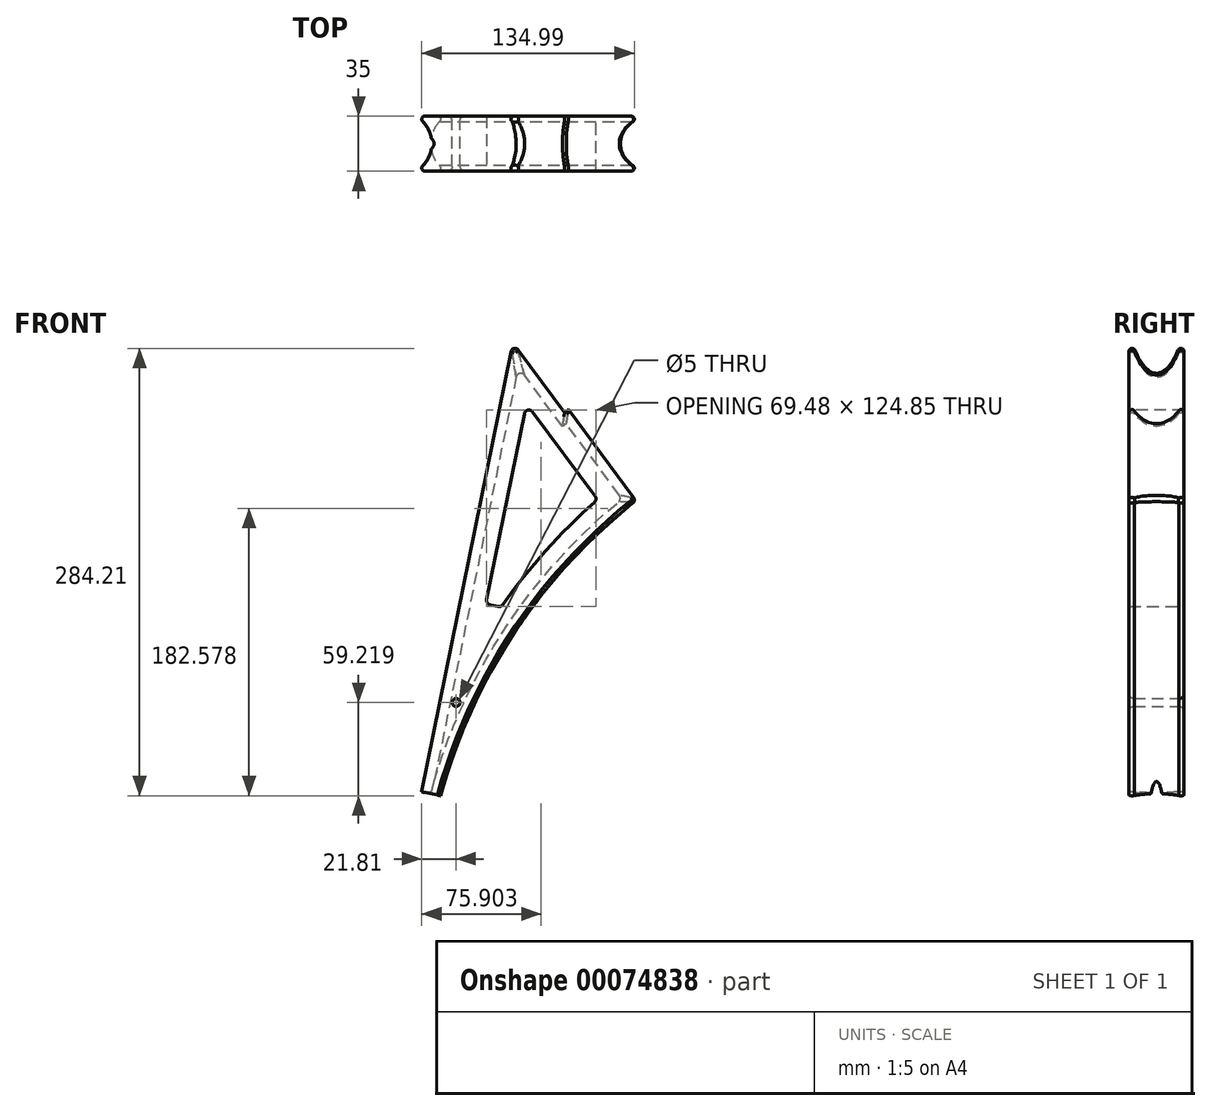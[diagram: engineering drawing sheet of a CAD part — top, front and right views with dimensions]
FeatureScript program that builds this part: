
annotation { "Feature Type Name" : "Feature", "Feature Type Description" : "" }
export const myFeature = defineFeature(function(context is Context, id is Id, definition is map)
    precondition{}
    {
        {
            var Q0;
            Q0=qCreatedBy(makeId("Front.planeOp"),FACE);
            var sketch = newSketch(context, id + "F0", { "sketchPlane" : qUnion([Q0])});
            skLineSegment(sketch, "E0", {"start": v(0, 0) * mm, "end": v(59.65, 294.01) * mm});
            skLineSegment(sketch, "E1", {"start": v(59.65, 294.01) * mm, "end": v(95.36, 245.8) * mm});
            skLineSegment(sketch, "E2", {"start": v(95.36, 245.8) * mm, "end": v(97.77, 247.59) * mm});
            skLineSegment(sketch, "E3", {"start": v(97.77, 247.59) * mm, "end": v(145.26, 183.48) * mm});
            skLineSegment(sketch, "E4", {"start": v(115.54, 184.96) * mm, "end": v(70.32, 246.01) * mm});
            skLineSegment(sketch, "E5", {"start": v(0, 0) * mm, "end": v(19.6, -3.98) * mm});
            skArc(sketch, "E6", {"start": v(145.26, 183.48) * mm, "mid": v(67.14, 100) * mm, "end": v(19.6, -3.98) * mm});
            skLineSegment(sketch, "E7", {"start": v(70.32, 246.01) * mm, "end": v(44.47, 118.6) * mm});
            skLineSegment(sketch, "E8", {"start": v(44.47, 118.6) * mm, "end": v(54.27, 116.62) * mm});
            skArc(sketch, "E9", {"start": v(115.54, 184.96) * mm, "mid": v(82.8, 152.67) * mm, "end": v(54.27, 116.62) * mm});
            skCircle(sketch, "E10", {"center": v(25.65, 56.02) * mm, "radius": 2.5 * mm});
            skSolve(sketch);
        }
        {
            var Q0;
            Q0 = qSketchRegion(id + "F0", true);
            extrude(context, id + "F1", {"entities" : qUnion([Q0]), "depth" : 35 * mm});
        }
        {
            var Q0;
            Q0=makeQuery(id+"F1.opExtrude","SWEPT_FACE",FACE,{"disambiguationData":[OSD([sQuery(id+"F0.wireOp",EDGE,"E5")])]});
            var sketch = newSketch(context, id + "F2", { "sketchPlane" : qUnion([Q0])});
            skArc(sketch, "E11", {"start": v(20, 35) * mm, "mid": v(9.68, 17.5) * mm, "end": v(20, 0) * mm});
            skLineSegment(sketch, "E12", {"start": v(20, 0) * mm, "end": v(20, 35) * mm});
            skSolve(sketch);
        }
        {
            var Q0;
            Q0=makeQuery(id+"F2.imprint","IMPRINT",FACE,{"disambiguationData":[TD([[makeQuery(id+"F2.imprint","IMPRINT",EDGE,{"derivedFrom":sQuery(id+"F2.wireOp",EDGE,"E11")}),1.0]])]});
            var Q1;
            Q1=makeQuery(id+"F1.opExtrude","CAP_EDGE",EDGE,{"disambiguationData":[OSD([sQuery(id+"F0.wireOp",EDGE,"E6")])],"isStart":true});
            var Q2;
            Q2=makeQuery(id+"F1.opExtrude","CAP_EDGE",EDGE,{"disambiguationData":[OSD([sQuery(id+"F0.wireOp",EDGE,"E3")])],"isStart":true});
            var Q3;
            Q3=makeQuery(id+"F1.opExtrude","CAP_EDGE",EDGE,{"disambiguationData":[OSD([sQuery(id+"F0.wireOp",EDGE,"E1")])],"isStart":true});
            var Q4;
            Q4=makeQuery(id+"F1.opExtrude","CAP_EDGE",EDGE,{"disambiguationData":[OSD([sQuery(id+"F0.wireOp",EDGE,"E2")])],"isStart":true});
            var Q5;
            Q5=makeQuery(id+"F1.opExtrude","CAP_EDGE",EDGE,{"disambiguationData":[OSD([sQuery(id+"F0.wireOp",EDGE,"E0")])],"isStart":true});
            sweep(context, id + "F3", {"operationType" : NewBodyOperationType.REMOVE, "profiles" : qUnion([Q0]), "path" : qUnion([Q1, Q2, Q3, Q4, Q5])});
        }
        {
            var Q0;
            Q0=makeQuery(id+"F3.boolean.opBoolean","COPY",FACE,{"derivedFrom":makeQuery(id+"F3.opSweep","CAP_FACE",FACE,{"disambiguationData":[OSD([sQuery(id+"F0.wireOp",EDGE,"E0"),sQuery(id+"F0.wireOp",EDGE,"E5"),sQuery(id+"F2.wireOp",EDGE,"E11"),sQuery(id+"F2.wireOp",EDGE,"E12")])],"isStart":false})});
            extrude(context, id + "F4", {"entities" : qUnion([Q0]), "operationType" : NewBodyOperationType.REMOVE, "oppositeDirection" : true, "depth" : 25 * mm});
        }
        {
            var Q0;
            {var subQ0=sQuery(id+"F2.wireOp",EDGE,"E12");var subQ1=sQuery(id+"F2.wireOp",EDGE,"E11");var subQ2=sQuery(id+"F0.wireOp",EDGE,"E5");var subQ3=sQuery(id+"F0.wireOp",EDGE,"E0");var subQ4=makeQuery(id+"F1.opExtrude","CAP_EDGE",EDGE,{"disambiguationData":[OSD([subQ3])],"isStart":true});Q0=makeQuery(id+"FQC8LGYjpT3Sznm_1.boolean.opBoolean","MERGE",EDGE,{"derivedFrom":[subQ4,makeQuery(id+"FQC8LGYjpT3Sznm_1.opSweep","SWEPT_EDGE",EDGE,{"disambiguationData":[OSD([subQ3,subQ2,subQ1,subQ0]),TDD([subQ4,makeQuery(id+"F2.imprint","INTERSECT",VERTEX,{"derivedFrom":[makeQuery(id+"F1.opExtrude","CAP_EDGE",EDGE,{"disambiguationData":[OSD([subQ2])],"isStart":true}),subQ1,subQ0]})])]})]});}
            var Q1;
            {var subQ0=sQuery(id+"F2.wireOp",EDGE,"E12");var subQ1=sQuery(id+"F2.wireOp",EDGE,"E11");var subQ2=sQuery(id+"F0.wireOp",EDGE,"E5");var subQ3=sQuery(id+"F0.wireOp",EDGE,"E0");Q1=makeQuery(id+"FQC8LGYjpT3Sznm_1.boolean.opBoolean","MERGE",EDGE,{"derivedFrom":[makeQuery(id+"F1.opExtrude","CAP_EDGE",EDGE,{"disambiguationData":[OSD([subQ3])],"isStart":false}),makeQuery(id+"FQC8LGYjpT3Sznm_1.opSweep","SWEPT_EDGE",EDGE,{"disambiguationData":[OSD([subQ3,subQ2,subQ1,subQ0]),TDD([makeQuery(id+"F1.opExtrude","CAP_EDGE",EDGE,{"disambiguationData":[OSD([subQ3])],"isStart":true}),makeQuery(id+"F2.imprint","INTERSECT",VERTEX,{"derivedFrom":[makeQuery(id+"F1.opExtrude","CAP_EDGE",EDGE,{"disambiguationData":[OSD([subQ2])],"isStart":false}),subQ1,subQ0]})])]})]});}
            var Q2;
            {var subQ0=sQuery(id+"F2.wireOp",EDGE,"E12");var subQ1=sQuery(id+"F2.wireOp",EDGE,"E11");var subQ2=sQuery(id+"F0.wireOp",EDGE,"E5");var subQ3=sQuery(id+"F0.wireOp",EDGE,"E6");Q2=makeQuery(id+"FQC8LGYjpT3Sznm_1.boolean.opBoolean","MERGE",EDGE,{"derivedFrom":[makeQuery(id+"F1.opExtrude","CAP_EDGE",EDGE,{"disambiguationData":[OSD([subQ3])],"isStart":false}),makeQuery(id+"FQC8LGYjpT3Sznm_1.opSweep","SWEPT_EDGE",EDGE,{"disambiguationData":[OSD([subQ2,subQ3,subQ1,subQ0]),TDD([makeQuery(id+"F1.opExtrude","CAP_EDGE",EDGE,{"disambiguationData":[OSD([subQ3])],"isStart":true}),makeQuery(id+"F2.imprint","INTERSECT",VERTEX,{"derivedFrom":[makeQuery(id+"F1.opExtrude","CAP_EDGE",EDGE,{"disambiguationData":[OSD([subQ2])],"isStart":false}),subQ1,subQ0]})])]})]});}
            var Q3;
            {var subQ0=sQuery(id+"F2.wireOp",EDGE,"E12");var subQ1=sQuery(id+"F2.wireOp",EDGE,"E11");var subQ2=sQuery(id+"F0.wireOp",EDGE,"E5");var subQ3=sQuery(id+"F0.wireOp",EDGE,"E6");var subQ4=makeQuery(id+"F1.opExtrude","CAP_EDGE",EDGE,{"disambiguationData":[OSD([subQ3])],"isStart":true});Q3=makeQuery(id+"FQC8LGYjpT3Sznm_1.boolean.opBoolean","MERGE",EDGE,{"derivedFrom":[subQ4,makeQuery(id+"FQC8LGYjpT3Sznm_1.opSweep","SWEPT_EDGE",EDGE,{"disambiguationData":[OSD([subQ2,subQ3,subQ1,subQ0]),TDD([subQ4,makeQuery(id+"F2.imprint","INTERSECT",VERTEX,{"derivedFrom":[makeQuery(id+"F1.opExtrude","CAP_EDGE",EDGE,{"disambiguationData":[OSD([subQ2])],"isStart":true}),subQ1,subQ0]})])]})]});}
            var Q4;
            {var subQ0=sQuery(id+"F2.wireOp",EDGE,"E12");var subQ1=sQuery(id+"F2.wireOp",EDGE,"E11");var subQ2=sQuery(id+"F0.wireOp",EDGE,"E5");var subQ3=sQuery(id+"F0.wireOp",EDGE,"E3");Q4=makeQuery(id+"FQC8LGYjpT3Sznm_1.boolean.opBoolean","MERGE",EDGE,{"derivedFrom":[makeQuery(id+"F1.opExtrude","CAP_EDGE",EDGE,{"disambiguationData":[OSD([subQ3])],"isStart":false}),makeQuery(id+"FQC8LGYjpT3Sznm_1.opSweep","SWEPT_EDGE",EDGE,{"disambiguationData":[OSD([subQ3,subQ2,subQ1,subQ0]),TDD([makeQuery(id+"F1.opExtrude","CAP_EDGE",EDGE,{"disambiguationData":[OSD([subQ3])],"isStart":true}),makeQuery(id+"F2.imprint","INTERSECT",VERTEX,{"derivedFrom":[makeQuery(id+"F1.opExtrude","CAP_EDGE",EDGE,{"disambiguationData":[OSD([subQ2])],"isStart":false}),subQ1,subQ0]})])]})]});}
            var Q5;
            {var subQ0=sQuery(id+"F2.wireOp",EDGE,"E12");var subQ1=sQuery(id+"F2.wireOp",EDGE,"E11");var subQ2=sQuery(id+"F0.wireOp",EDGE,"E5");var subQ3=sQuery(id+"F0.wireOp",EDGE,"E3");var subQ4=makeQuery(id+"F1.opExtrude","CAP_EDGE",EDGE,{"disambiguationData":[OSD([subQ3])],"isStart":true});Q5=makeQuery(id+"FQC8LGYjpT3Sznm_1.boolean.opBoolean","MERGE",EDGE,{"derivedFrom":[subQ4,makeQuery(id+"FQC8LGYjpT3Sznm_1.opSweep","SWEPT_EDGE",EDGE,{"disambiguationData":[OSD([subQ3,subQ2,subQ1,subQ0]),TDD([subQ4,makeQuery(id+"F2.imprint","INTERSECT",VERTEX,{"derivedFrom":[makeQuery(id+"F1.opExtrude","CAP_EDGE",EDGE,{"disambiguationData":[OSD([subQ2])],"isStart":true}),subQ1,subQ0]})])]})]});}
            var Q6;
            {var subQ0=sQuery(id+"F2.wireOp",EDGE,"E12");var subQ1=sQuery(id+"F2.wireOp",EDGE,"E11");var subQ2=sQuery(id+"F0.wireOp",EDGE,"E5");var subQ3=sQuery(id+"F0.wireOp",EDGE,"E1");Q6=makeQuery(id+"FQC8LGYjpT3Sznm_1.boolean.opBoolean","MERGE",EDGE,{"derivedFrom":[makeQuery(id+"F1.opExtrude","CAP_EDGE",EDGE,{"disambiguationData":[OSD([subQ3])],"isStart":false}),makeQuery(id+"FQC8LGYjpT3Sznm_1.opSweep","SWEPT_EDGE",EDGE,{"disambiguationData":[OSD([subQ3,subQ2,subQ1,subQ0]),TDD([makeQuery(id+"F1.opExtrude","CAP_EDGE",EDGE,{"disambiguationData":[OSD([subQ3])],"isStart":true}),makeQuery(id+"F2.imprint","INTERSECT",VERTEX,{"derivedFrom":[makeQuery(id+"F1.opExtrude","CAP_EDGE",EDGE,{"disambiguationData":[OSD([subQ2])],"isStart":false}),subQ1,subQ0]})])]})]});}
            var Q7;
            {var subQ0=sQuery(id+"F2.wireOp",EDGE,"E12");var subQ1=sQuery(id+"F2.wireOp",EDGE,"E11");var subQ2=sQuery(id+"F0.wireOp",EDGE,"E5");var subQ3=sQuery(id+"F0.wireOp",EDGE,"E1");var subQ4=makeQuery(id+"F1.opExtrude","CAP_EDGE",EDGE,{"disambiguationData":[OSD([subQ3])],"isStart":true});Q7=makeQuery(id+"FQC8LGYjpT3Sznm_1.boolean.opBoolean","MERGE",EDGE,{"derivedFrom":[subQ4,makeQuery(id+"FQC8LGYjpT3Sznm_1.opSweep","SWEPT_EDGE",EDGE,{"disambiguationData":[OSD([subQ3,subQ2,subQ1,subQ0]),TDD([subQ4,makeQuery(id+"F2.imprint","INTERSECT",VERTEX,{"derivedFrom":[makeQuery(id+"F1.opExtrude","CAP_EDGE",EDGE,{"disambiguationData":[OSD([subQ2])],"isStart":true}),subQ1,subQ0]})])]})]});}
            var Q8;
            {var subQ0=sQuery(id+"F2.wireOp",EDGE,"E12");var subQ1=sQuery(id+"F2.wireOp",EDGE,"E11");var subQ2=sQuery(id+"F0.wireOp",EDGE,"E5");var subQ3=sQuery(id+"F0.wireOp",EDGE,"E2");Q8=makeQuery(id+"FQC8LGYjpT3Sznm_1.boolean.opBoolean","MERGE",EDGE,{"derivedFrom":[makeQuery(id+"F1.opExtrude","CAP_EDGE",EDGE,{"disambiguationData":[OSD([subQ3])],"isStart":false}),makeQuery(id+"FQC8LGYjpT3Sznm_1.opSweep","SWEPT_EDGE",EDGE,{"disambiguationData":[OSD([subQ3,subQ2,subQ1,subQ0]),TDD([makeQuery(id+"F1.opExtrude","CAP_EDGE",EDGE,{"disambiguationData":[OSD([subQ3])],"isStart":true}),makeQuery(id+"F2.imprint","INTERSECT",VERTEX,{"derivedFrom":[makeQuery(id+"F1.opExtrude","CAP_EDGE",EDGE,{"disambiguationData":[OSD([subQ2])],"isStart":false}),subQ1,subQ0]})])]})]});}
            var Q9;
            {var subQ0=sQuery(id+"F2.wireOp",EDGE,"E12");var subQ1=sQuery(id+"F2.wireOp",EDGE,"E11");var subQ2=sQuery(id+"F0.wireOp",EDGE,"E5");var subQ3=sQuery(id+"F0.wireOp",EDGE,"E2");var subQ4=makeQuery(id+"F1.opExtrude","CAP_EDGE",EDGE,{"disambiguationData":[OSD([subQ3])],"isStart":true});Q9=makeQuery(id+"FQC8LGYjpT3Sznm_1.boolean.opBoolean","MERGE",EDGE,{"derivedFrom":[subQ4,makeQuery(id+"FQC8LGYjpT3Sznm_1.opSweep","SWEPT_EDGE",EDGE,{"disambiguationData":[OSD([subQ3,subQ2,subQ1,subQ0]),TDD([subQ4,makeQuery(id+"F2.imprint","INTERSECT",VERTEX,{"derivedFrom":[makeQuery(id+"F1.opExtrude","CAP_EDGE",EDGE,{"disambiguationData":[OSD([subQ2])],"isStart":true}),subQ1,subQ0]})])]})]});}
            fillet(context, id + "F5", {"entities" : qUnion([Q0, Q1, Q2, Q3, Q4, Q5, Q6, Q7, Q8, Q9]), "radius" : 2 * mm, "tangentPropagation" : true, "allowEdgeOverflow" : false});
        }
        {
            var Q0;
            Q0=makeQuery(id+"F3.boolean.opBoolean","COPY",EDGE,{"derivedFrom":makeQuery(id+"F3.opSweep","MID_CAP_EDGE",EDGE,{"disambiguationData":[OSD([sQuery(id+"F0.wireOp",EDGE,"E3"),sQuery(id+"F0.wireOp",EDGE,"E6"),sQuery(id+"F2.wireOp",EDGE,"E11")])],"capPos":1.0})});
            var Q1;
            Q1=makeQuery(id+"F3.boolean.opBoolean","COPY",EDGE,{"derivedFrom":makeQuery(id+"F3.opSweep","MID_CAP_EDGE",EDGE,{"disambiguationData":[OSD([sQuery(id+"F0.wireOp",EDGE,"E0"),sQuery(id+"F0.wireOp",EDGE,"E1"),sQuery(id+"F2.wireOp",EDGE,"E11")])],"capPos":4.0})});
            fillet(context, id + "F6", {"entities" : qUnion([Q0, Q1]), "radius" : 3 * mm, "tangentPropagation" : true, "allowEdgeOverflow" : false});
        }
        {
            var Q0;
            Q0=makeQuery(id+"F1.opExtrude","SWEPT_EDGE",EDGE,{"disambiguationData":[OSD([sQuery(id+"F0.wireOp",EDGE,"E4"),sQuery(id+"F0.wireOp",EDGE,"E7")])]});
            var Q1;
            Q1=makeQuery(id+"F1.opExtrude","SWEPT_EDGE",EDGE,{"disambiguationData":[OSD([sQuery(id+"F0.wireOp",EDGE,"E4"),sQuery(id+"F0.wireOp",EDGE,"E9")])]});
            var Q2;
            Q2=makeQuery(id+"F1.opExtrude","SWEPT_EDGE",EDGE,{"disambiguationData":[OSD([sQuery(id+"F0.wireOp",EDGE,"E7"),sQuery(id+"F0.wireOp",EDGE,"E8")])]});
            var Q3;
            Q3=makeQuery(id+"F1.opExtrude","SWEPT_EDGE",EDGE,{"disambiguationData":[OSD([sQuery(id+"F0.wireOp",EDGE,"E8"),sQuery(id+"F0.wireOp",EDGE,"E9")])]});
            fillet(context, id + "F7", {"entities" : qUnion([Q0, Q1, Q2, Q3]), "radius" : 3 * mm, "tangentPropagation" : true, "allowEdgeOverflow" : false});
        }
        {
            var Q0;
            Q0=makeQuery(id+"F1.opExtrude","CAP_EDGE",EDGE,{"disambiguationData":[OSD([sQuery(id+"F0.wireOp",EDGE,"E10")])],"isStart":false});
            var Q1;
            Q1=makeQuery(id+"F1.opExtrude","CAP_EDGE",EDGE,{"disambiguationData":[OSD([sQuery(id+"F0.wireOp",EDGE,"E10")])],"isStart":true});
            fillet(context, id + "F8", {"entities" : qUnion([Q0, Q1]), "radius" : 3 * mm, "tangentPropagation" : true, "allowEdgeOverflow" : false});
        }
    });
